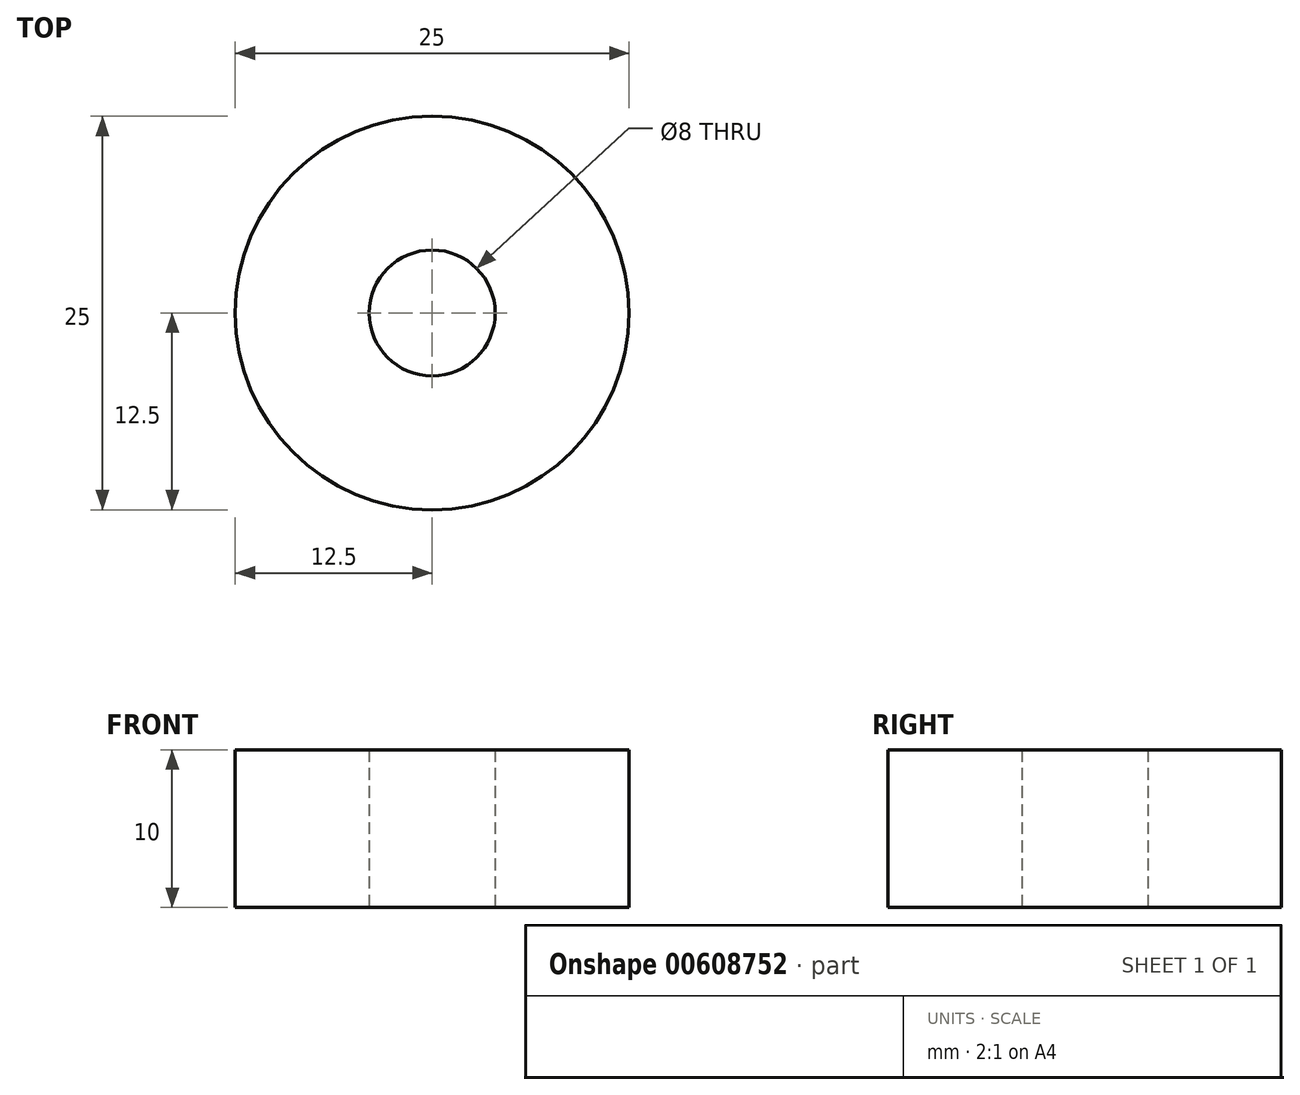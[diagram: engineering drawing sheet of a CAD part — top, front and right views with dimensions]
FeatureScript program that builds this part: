
annotation { "Feature Type Name" : "Feature", "Feature Type Description" : "" }
export const myFeature = defineFeature(function(context is Context, id is Id, definition is map)
    precondition{}
    {
        {
            var Q0;
            Q0=qCreatedBy(makeId("Top.planeOp"),FACE);
            var sketch = newSketch(context, id + "F0", { "sketchPlane" : qUnion([Q0])});
            skCircle(sketch, "E0", {"center": v(0, 0) * mm, "radius": 12.5 * mm});
            skCircle(sketch, "E1", {"center": v(0, 0) * mm, "radius": 4 * mm});
            skSolve(sketch);
        }
        {
            var Q0;
            Q0=makeQuery(id+"F0.imprint","IMPRINT",FACE,{"disambiguationData":[TD([[makeQuery(id+"F0.imprint","IMPRINT",EDGE,{"derivedFrom":sQuery(id+"F0.wireOp",EDGE,"E0")}),1.0]])]});
            extrude(context, id + "F1", {"entities" : qUnion([Q0]), "depth" : 10 * mm, "offsetDistance" : 25 * mm});
        }
    });
